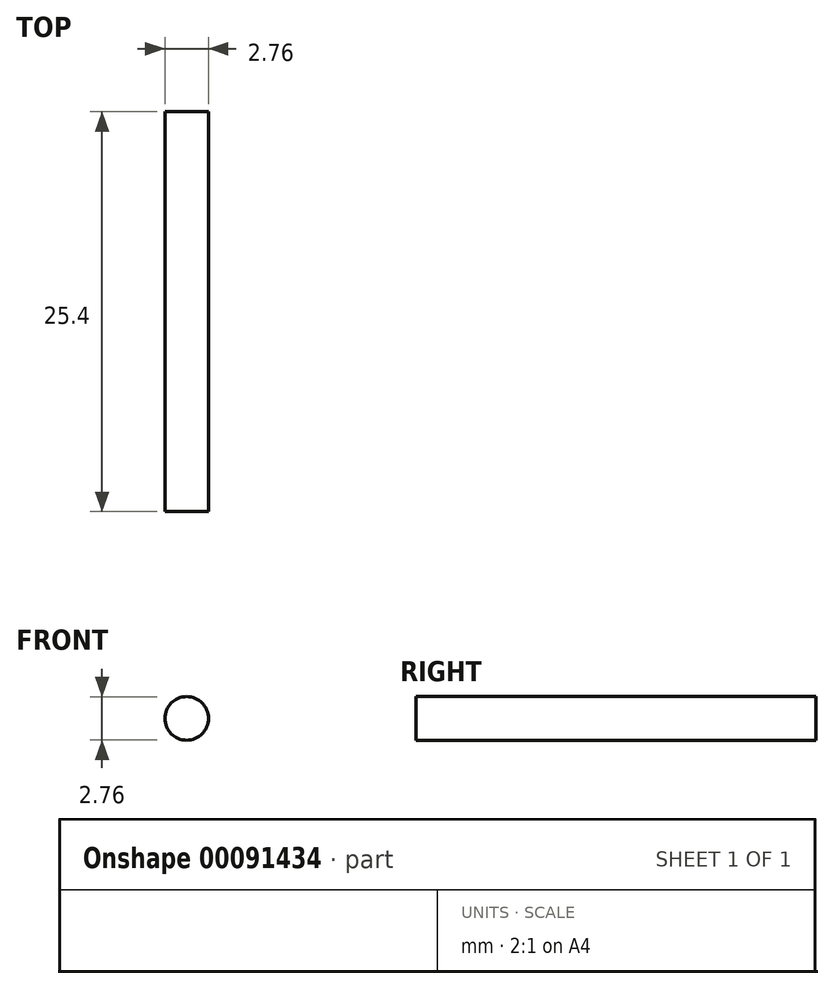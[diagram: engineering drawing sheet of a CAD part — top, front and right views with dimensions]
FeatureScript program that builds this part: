
annotation { "Feature Type Name" : "Feature", "Feature Type Description" : "" }
export const myFeature = defineFeature(function(context is Context, id is Id, definition is map)
    precondition{}
    {
        {
            var Q0;
            Q0=qCreatedBy(makeId("Front.planeOp"),FACE);
            var sketch = newSketch(context, id + "F0", { "sketchPlane" : qUnion([Q0])});
            skCircle(sketch, "E0", {"center": v(0, 0) * mm, "radius": 1.38 * mm});
            skSolve(sketch);
        }
        {
            var Q0;
            Q0 = qSketchRegion(id + "F0", true);
            extrude(context, id + "F1", {"entities" : qUnion([Q0]), "depth" : 25.4 * mm});
        }
    });
